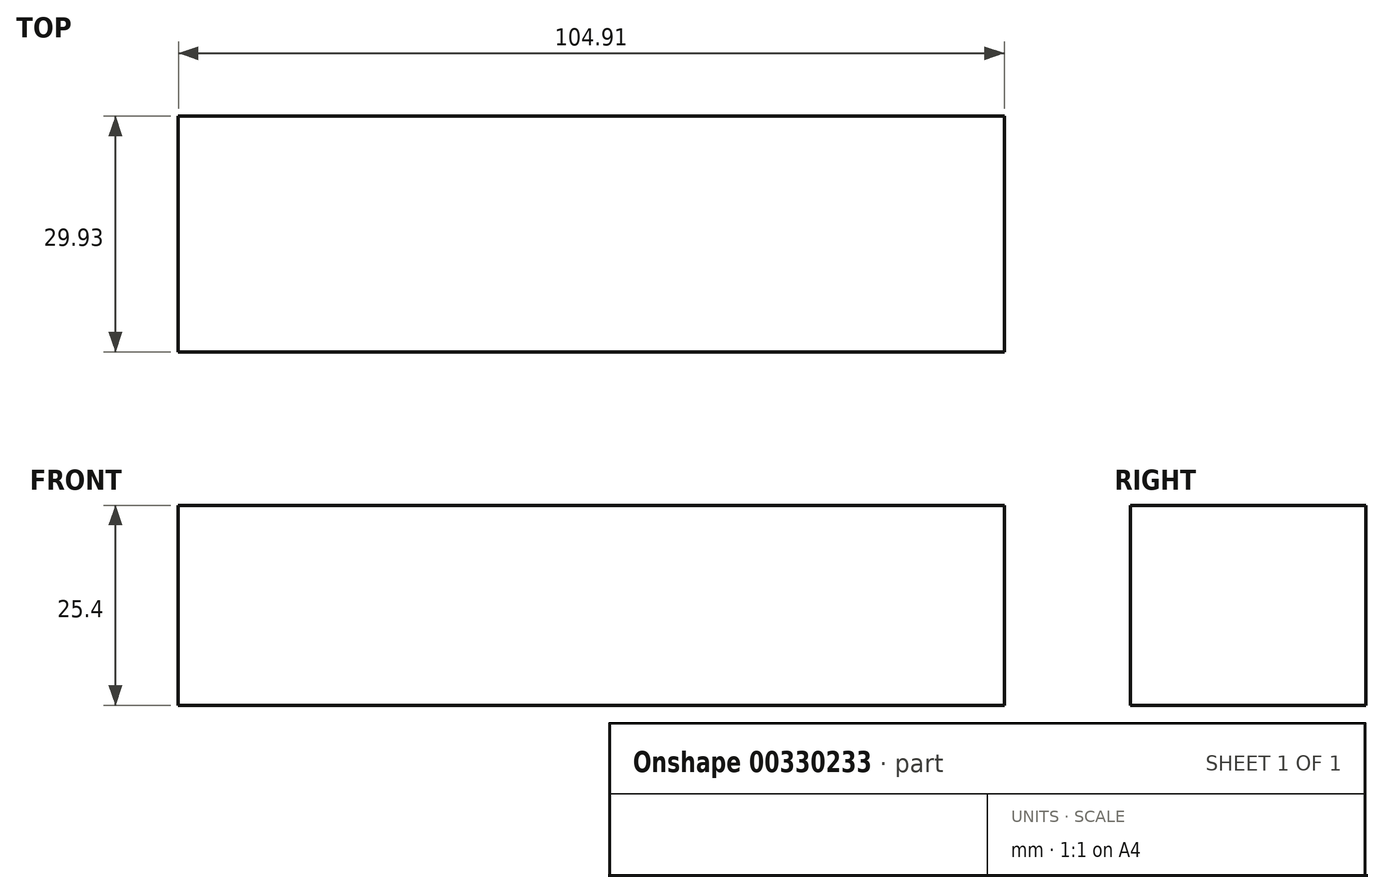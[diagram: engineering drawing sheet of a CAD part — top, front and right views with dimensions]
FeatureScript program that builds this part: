
annotation { "Feature Type Name" : "Feature", "Feature Type Description" : "" }
export const myFeature = defineFeature(function(context is Context, id is Id, definition is map)
    precondition{}
    {
        {
            var Q0;
            Q0=qCreatedBy(makeId("Top.planeOp"),FACE);
            var sketch = newSketch(context, id + "F0", { "sketchPlane" : qUnion([Q0])});
            skLineSegment(sketch, "E0.bottom", {"start": v(-53.57, -13.43) * mm, "end": v(51.34, -13.43) * mm});
            skLineSegment(sketch, "E0.top", {"start": v(-53.57, -43.36) * mm, "end": v(51.34, -43.36) * mm});
            skLineSegment(sketch, "E0.left", {"start": v(-53.57, -13.43) * mm, "end": v(-53.57, -43.36) * mm});
            skLineSegment(sketch, "E0.right", {"start": v(51.34, -13.43) * mm, "end": v(51.34, -43.36) * mm});
            skSolve(sketch);
        }
        {
            var Q0;
            Q0=makeQuery(id+"F0.imprint","IMPRINT",FACE,{"disambiguationData":[TD([[makeQuery(id+"F0.imprint","IMPRINT",EDGE,{"derivedFrom":sQuery(id+"F0.wireOp",EDGE,"E0.bottom")}),-1.0]])]});
            extrude(context, id + "F1", {"entities" : qUnion([Q0]), "depth" : 25.4 * mm});
        }
    });
